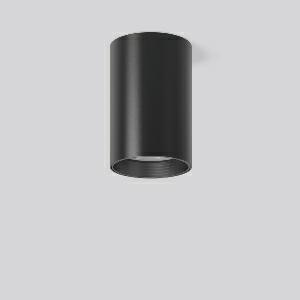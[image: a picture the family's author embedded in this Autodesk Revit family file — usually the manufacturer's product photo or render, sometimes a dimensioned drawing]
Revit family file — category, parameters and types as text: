
# Revit family: heledon_maxi_a_931236_003_76_330f
name_source: partatom
category: Lighting Fixtures
units: mm (PartAtom-declared; Revit-internal decimal feet)

## family parameters
Cut with Voids When Loaded = No
Host = Face
Light Source = No
Part Type = Normal
Room Calculation Point = No
Round Connector Dimension = Use Diameter
Shared = No

## types (1)
- HELEDON maxi A (1 x LED Modul 932 fresh meat, 1800 lm, 3200)
    Apparent Load = 33 VA
    Approval mark = CE
    CIE Flux Codes = 96 99 100 100 100
    Color Rendering = 90
    Color Temperature = 3200
    Default Elevation = 1800 mm  [stored 5.90551 ft]
    Description = Series: HELEDON maxi
Cylindrical surface-mounted downlight. Housing: die-cast aluminium, powder-coated. Internal ceiling frame polycarbonate with bayonet mounting. Black plastic ring and recessed LED to prevent glare from the side. Optical assembly with lens made of plastic (polycarbonate) for the best homogeneous light distribution - can be changed without tools. Special LED for illumination of meat included. Suitable for Ceiling mounting. Easy installation with a separate ceiling frame with bayonet mounting and plug connection. Driver integrated. Connected via plug-in connector. High quality converter without flickering and stroboscopic effect. The following accessories can be mounted without use of tools: interchangeable lenses, decorative glasses, honeycomb louvre, clear and frosted diffusers, white interchangeable plastic ring. 
Colour: deep black, matt (RAL 9005)
Diameter: 123 mm
Height: 183 mm
Lamp: LED
Socket: without socket
Colour temperature: fresh meat
System power: 33 W
Rated luminous flux: 1800 lm
Luminous efficiency: 55 lm/W
Control gear: Converter, dimmable, DALI
Protection class: I
Type of protection: IP 20
    Height = 183 mm
    Lamp = 1 x LED Modul 932 fresh meat
    Lamp Light Flux = 1800 lm
    Lamp count = 1
    Length = 123 mm
    Lifetime = 50000 h
    Luminous efficacy = 55 lm/W
    Manufacturer = RZB
    ModVariant = No
    Model = 931236.003.76
    Mounting Place = Ceiling
    Mounting Type = Surface mounted
    Number of Poles = 1
    OnlyDefault = Yes
    Power Factor = 1
    Product Name = HELEDON maxi A
    Product group = Surface mounted downlights
    ProductGroupID = 302
    Protection Class = Protection class I
    Protection Degree = IP 20
    RLX_Detail_Level = 1
    RLX_Emergency_Light_Flux = 0 lm
    RLX_Emergency_Type = 0
    RLX_Emergency_Type_DB = No
    RlxData = <blob elided: 95925 chars, md5=d4e250f7>
    Socket = socket
    Standby Power = 0 W
    System Light Flux = 1800 lm
    System Power = 33 W
    Type Comments = Product without accessories
    Type Image = 931193.003.jpg
    URL = http://relux.com
    VarID = ---
    Voltage = 230 V
    Voltage Range = 220-240 V
    Weight = 0.00 kg
    Width = 0 mm  [stored 0 ft]

note: [stored X ft] marks values corroborated as IEEE doubles in the binary element streams (Revit-internal decimal feet)

## geometry (parser evidence)
native form markers: Blend x4, Sweep x8
no freeform markers — native parametric forms only
